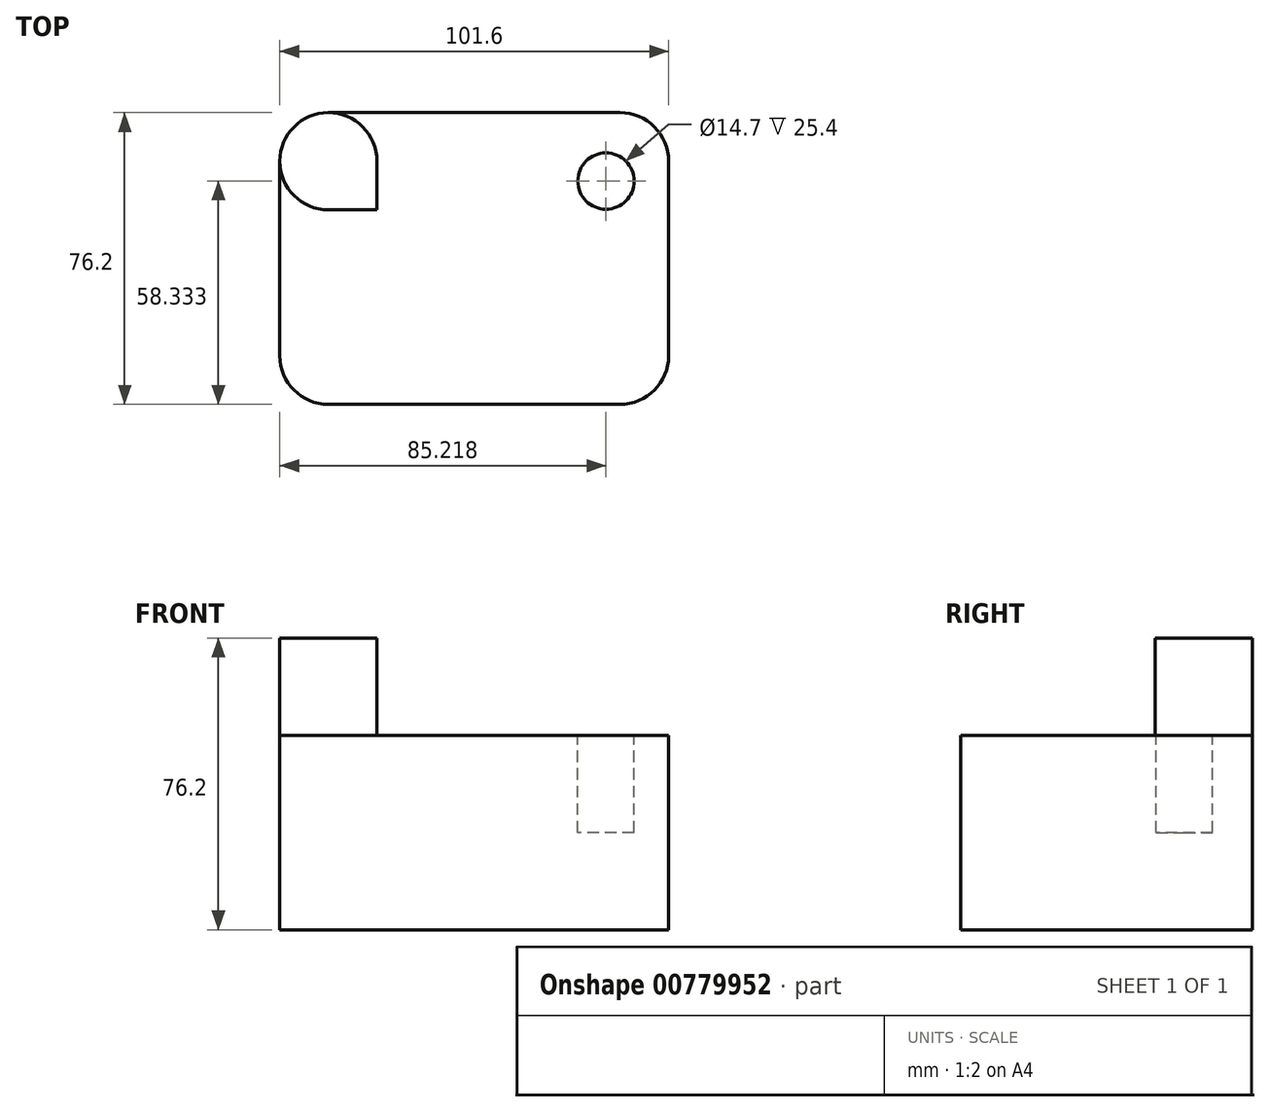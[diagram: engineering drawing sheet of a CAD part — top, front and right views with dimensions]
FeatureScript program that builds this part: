
annotation { "Feature Type Name" : "Feature", "Feature Type Description" : "" }
export const myFeature = defineFeature(function(context is Context, id is Id, definition is map)
    precondition{}
    {
        {
            var Q0;
            Q0=qCreatedBy(makeId("Top.planeOp"),FACE);
            var sketch = newSketch(context, id + "F0", { "sketchPlane" : qUnion([Q0])});
            skLineSegment(sketch, "E0.bottom", {"start": v(0, 0) * mm, "end": v(101.6, 0) * mm});
            skLineSegment(sketch, "E0.top", {"start": v(0, 76.2) * mm, "end": v(101.6, 76.2) * mm});
            skLineSegment(sketch, "E0.left", {"start": v(0, 0) * mm, "end": v(0, 76.2) * mm});
            skLineSegment(sketch, "E0.right", {"start": v(101.6, 0) * mm, "end": v(101.6, 76.2) * mm});
            skSolve(sketch);
        }
        {
            var Q0;
            Q0=makeQuery(id+"F0.imprint","IMPRINT",FACE,{"disambiguationData":[TD([[makeQuery(id+"F0.imprint","IMPRINT",EDGE,{"derivedFrom":sQuery(id+"F0.wireOp",EDGE,"E0.bottom")}),1.0]])]});
            extrude(context, id + "F1", {"entities" : qUnion([Q0]), "depth" : 50.8 * mm, "offsetDistance" : 25.4 * mm});
        }
        {
            var Q0;
            Q0=makeQuery(id+"F1.opExtrude","SWEPT_EDGE",EDGE,{"disambiguationData":[OSD([sQuery(id+"F0.wireOp",EDGE,"E0.bottom"),sQuery(id+"F0.wireOp",EDGE,"E0.left")])]});
            var Q1;
            Q1=makeQuery(id+"F1.opExtrude","SWEPT_EDGE",EDGE,{"disambiguationData":[OSD([sQuery(id+"F0.wireOp",EDGE,"E0.bottom"),sQuery(id+"F0.wireOp",EDGE,"E0.right")])]});
            var Q2;
            Q2=makeQuery(id+"F1.opExtrude","SWEPT_EDGE",EDGE,{"disambiguationData":[OSD([sQuery(id+"F0.wireOp",EDGE,"E0.top"),sQuery(id+"F0.wireOp",EDGE,"E0.right")])]});
            var Q3;
            Q3=makeQuery(id+"F1.opExtrude","SWEPT_EDGE",EDGE,{"disambiguationData":[OSD([sQuery(id+"F0.wireOp",EDGE,"E0.top"),sQuery(id+"F0.wireOp",EDGE,"E0.left")])]});
            fillet(context, id + "F2", {"entities" : qUnion([Q0, Q1, Q2, Q3]), "radius" : 12.7 * mm, "tangentPropagation" : true, "allowEdgeOverflow" : false});
        }
        {
            var Q0;
            Q0=makeQuery(id+"F1.opExtrude","CAP_FACE",FACE,{"disambiguationData":[OSD([sQuery(id+"F0.wireOp",EDGE,"E0.bottom"),sQuery(id+"F0.wireOp",EDGE,"E0.top"),sQuery(id+"F0.wireOp",EDGE,"E0.left"),sQuery(id+"F0.wireOp",EDGE,"E0.right")])],"isStart":false});
            var sketch = newSketch(context, id + "F3", { "sketchPlane" : qUnion([Q0])});
            skArc(sketch, "E1", {"start": v(12.7, 50.8) * mm, "mid": v(3.72, 72.48) * mm, "end": v(25.4, 63.5) * mm});
            skPoint(sketch, "E2", {"position": v(3.72, 72.48) * mm});
            skLineSegment(sketch, "E3", {"start": v(12.7, 0) * mm, "end": v(12.7, 63.5) * mm, "construction": true});
            skLineSegment(sketch, "E4", {"start": v(12.7, 63.5) * mm, "end": v(101.6, 63.5) * mm, "construction": true});
            skLineSegment(sketch, "E5", {"start": v(12.7, 50.8) * mm, "end": v(25.4, 50.8) * mm});
            skLineSegment(sketch, "E6", {"start": v(25.4, 50.8) * mm, "end": v(25.4, 63.5) * mm});
            skSolve(sketch);
        }
        {
            var Q0;
            {var subQ0=sQuery(id+"F3.wireOp",EDGE,"E5");Q0=makeQuery(id+"F3.imprint","IMPRINT",FACE,{"disambiguationData":[TD([[makeQuery(id+"F3.imprint","IMPRINT",EDGE,{"derivedFrom":subQ0}),1.0]])]});}
            extrude(context, id + "F4", {"entities" : qUnion([Q0]), "operationType" : NewBodyOperationType.ADD, "depth" : 25.4 * mm, "offsetDistance" : 25.4 * mm});
        }
        {
            var Q0;
            Q0=makeQuery(id+"F1.opExtrude","CAP_FACE",FACE,{"disambiguationData":[OSD([sQuery(id+"F0.wireOp",EDGE,"E0.bottom"),sQuery(id+"F0.wireOp",EDGE,"E0.top"),sQuery(id+"F0.wireOp",EDGE,"E0.left"),sQuery(id+"F0.wireOp",EDGE,"E0.right")])],"isStart":false});
            var sketch = newSketch(context, id + "F5", { "sketchPlane" : qUnion([Q0])});
            skLineSegment(sketch, "E7", {"start": v(0, 38.1) * mm, "end": v(101.6, 38.1) * mm});
            skSolve(sketch);
        }
        {
            var Q0;
            Q0=sQuery(id+"F5.wireOp",EDGE,"E7");
            cPlane(context, id + "F6", {"entities" : qUnion([Q0]), "cplaneType" : CPlaneType.LINE_ANGLE, "offset" : 25.4 * mm, "angle" : 0 * degree, "width" : 152.4 * mm, "height" : 152.4 * mm});
        }
        {
            var Q0;
            Q0=qCreatedBy(id+"F6.planeOp",FACE);
            var sketch = newSketch(context, id + "F7", { "sketchPlane" : qUnion([Q0])});
            skArc(sketch, "E8", {"start": v(-76.2, 50.8) * mm, "mid": v(-68.76, 68.76) * mm, "end": v(-50.8, 76.2) * mm});
            skLineSegment(sketch, "E9", {"start": v(-50.8, 50.8) * mm, "end": v(-50.8, 76.2) * mm, "construction": true});
            skSolve(sketch);
        }
        {
            var Q0;
            Q0=sQuery(id+"F7.wireOp",EDGE,"E8");
            var Q1;
            Q1=sQuery(id+"F7.wireOp",EDGE,"E9");
            revolve(context, id + "F8", {"bodyType" : ToolBodyType.SURFACE, "surfaceOperationType" : NewSurfaceOperationType.NEW, "surfaceEntities" : qUnion([Q0]), "axis" : qUnion([Q1]), "revolveType" : RevolveType.FULL});
        }
        {
            var Q0;
            {var subQ6=sQuery(id+"F5.wireOp",EDGE,"E7");Q0=makeQuery(id+"F5.imprint","IMPRINT",FACE,{"disambiguationData":[TD([[makeQuery(id+"F5.imprint","IMPRINT",EDGE,{"derivedFrom":subQ6}),1.0]])]});}
            var sketch = newSketch(context, id + "F9", { "sketchPlane" : qUnion([Q0])});
            skCircle(sketch, "E10", {"center": v(85.22, 58.33) * mm, "radius": 7.35 * mm});
            skSolve(sketch);
        }
        {
            var Q0;
            Q0 = qSketchRegion(id + "F9", true);
            extrude(context, id + "F10", {"entities" : qUnion([Q0]), "operationType" : NewBodyOperationType.REMOVE, "oppositeDirection" : true, "depth" : 25.4 * mm, "offsetDistance" : 25.4 * mm});
        }
    });
